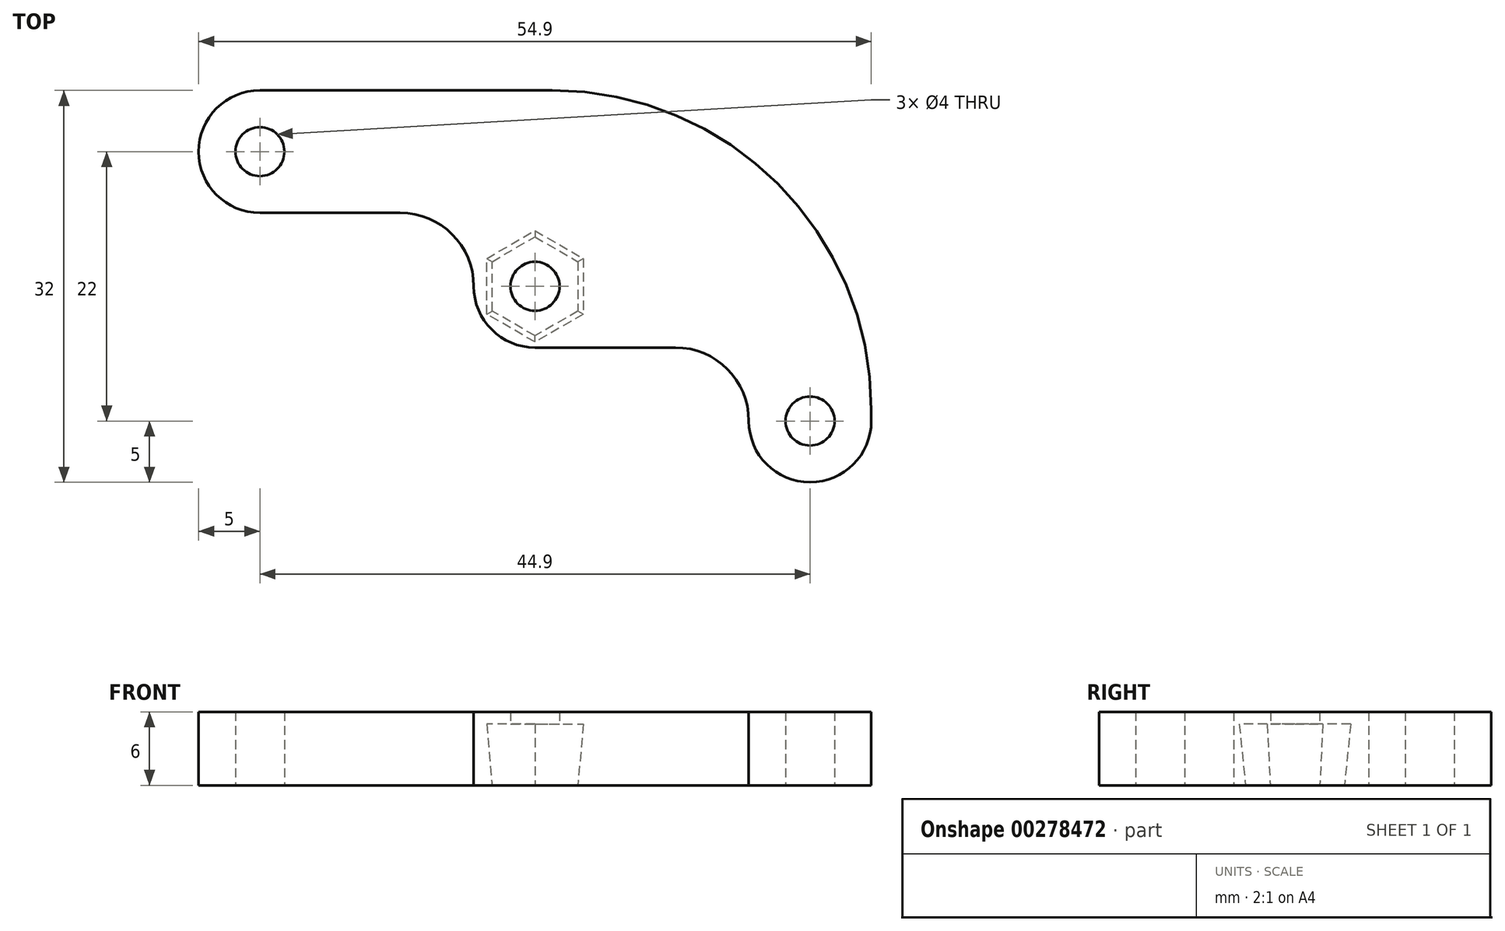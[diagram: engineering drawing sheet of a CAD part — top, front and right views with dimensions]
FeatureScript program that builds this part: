
annotation { "Feature Type Name" : "Feature", "Feature Type Description" : "" }
export const myFeature = defineFeature(function(context is Context, id is Id, definition is map)
    precondition{}
    {
        {
            var Q0;
            Q0=qCreatedBy(makeId("Top.planeOp"),FACE);
            var sketch = newSketch(context, id + "F0", { "sketchPlane" : qUnion([Q0])});
            skCircle(sketch, "E0", {"center": v(0, 0) * mm, "radius": 2 * mm});
            skCircle(sketch, "E1", {"center": v(22.45, -11) * mm, "radius": 2 * mm});
            skCircle(sketch, "E2", {"center": v(-22.45, 11) * mm, "radius": 2 * mm});
            skLineSegment(sketch, "E3", {"start": v(0, 16) * mm, "end": v(0, 6) * mm, "construction": true});
            skLineSegment(sketch, "E4", {"start": v(0, 6) * mm, "end": v(0, -6) * mm, "construction": true});
            skLineSegment(sketch, "E5", {"start": v(0, -6) * mm, "end": v(0, -16) * mm, "construction": true});
            skLineSegment(sketch, "E6", {"start": v(0, 11) * mm, "end": v(-22.45, 11) * mm, "construction": true});
            skLineSegment(sketch, "E7", {"start": v(0, -11) * mm, "end": v(22.45, -11) * mm, "construction": true});
            skCircle(sketch, "E8", {"center": v(-22.45, 11) * mm, "radius": 5 * mm, "construction": true});
            skCircle(sketch, "E9", {"center": v(0, 0) * mm, "radius": 5 * mm, "construction": true});
            skCircle(sketch, "E10", {"center": v(22.45, -11) * mm, "radius": 5 * mm, "construction": true});
            skLineSegment(sketch, "E11", {"start": v(-22.45, 6) * mm, "end": v(-11, 6) * mm});
            skLineSegment(sketch, "E12", {"start": v(-22.45, 16) * mm, "end": v(1.4, 16) * mm});
            skArc(sketch, "E13", {"start": v(-5, 0) * mm, "mid": v(-6.76, 4.24) * mm, "end": v(-11, 6) * mm});
            skArc(sketch, "E14", {"start": v(17.45, -11) * mm, "mid": v(22.45, -16) * mm, "end": v(27.45, -11) * mm});
            skArc(sketch, "E15", {"start": v(-22.45, 16) * mm, "mid": v(-27.45, 11) * mm, "end": v(-22.45, 6) * mm});
            skArc(sketch, "E16", {"start": v(-5, 0) * mm, "mid": v(-3.54, -3.54) * mm, "end": v(0, -5) * mm});
            skLineSegment(sketch, "E17", {"start": v(0, -5) * mm, "end": v(11.45, -5) * mm});
            skArc(sketch, "E18", {"start": v(17.45, -11) * mm, "mid": v(15.7, -6.76) * mm, "end": v(11.45, -5) * mm});
            skLineSegment(sketch, "E19", {"start": v(0, 5) * mm, "end": v(0, 5) * mm});
            skArc(sketch, "E20", {"start": v(27.45, -10.05) * mm, "mid": v(19.82, 8.37) * mm, "end": v(1.4, 16) * mm});
            skLineSegment(sketch, "E21", {"start": v(27.45, -11) * mm, "end": v(27.45, -10.05) * mm});
            skSolve(sketch);
        }
        {
            var Q0;
            Q0=qSketchRegion(id+"F0",true);
            extrude(context, id + "F1", {"entities" : qUnion([Q0]), "depth" : 6 * mm});
        }
        {
            var Q0;
            Q0=makeQuery(id+"F1.opExtrude","CAP_FACE",FACE,{"disambiguationData":[OSD([sQuery(id+"F0.wireOp",EDGE,"E0"),sQuery(id+"F0.wireOp",EDGE,"E1"),sQuery(id+"F0.wireOp",EDGE,"E2"),sQuery(id+"F0.wireOp",EDGE,"E11"),sQuery(id+"F0.wireOp",EDGE,"E12"),sQuery(id+"F0.wireOp",EDGE,"E13"),sQuery(id+"F0.wireOp",EDGE,"E14"),sQuery(id+"F0.wireOp",EDGE,"E15"),sQuery(id+"F0.wireOp",EDGE,"E16"),sQuery(id+"F0.wireOp",EDGE,"E17"),sQuery(id+"F0.wireOp",EDGE,"E18"),sQuery(id+"F0.wireOp",EDGE,"E20"),sQuery(id+"F0.wireOp",EDGE,"E21")])],"isStart":true});
            var sketch = newSketch(context, id + "F2", { "sketchPlane" : qUnion([Q0])});
            skCircle(sketch, "E22.cCircle", {"center": v(0, 0) * mm, "radius": 3.5 * mm, "construction": true});
            skLineSegment(sketch, "E22.0", {"start": v(3.5, -2.02) * mm, "end": v(0, -4.04) * mm});
            skLineSegment(sketch, "E22.1", {"start": v(0, -4.04) * mm, "end": v(-3.5, -2.02) * mm});
            skLineSegment(sketch, "E22.2", {"start": v(-3.5, -2.02) * mm, "end": v(-3.5, 2.02) * mm});
            skLineSegment(sketch, "E22.3", {"start": v(-3.5, 2.02) * mm, "end": v(0, 4.04) * mm});
            skLineSegment(sketch, "E22.4", {"start": v(0, 4.04) * mm, "end": v(3.5, 2.02) * mm});
            skLineSegment(sketch, "E22.5", {"start": v(3.5, 2.02) * mm, "end": v(3.5, -2.02) * mm});
            skPoint(sketch, "E22.0.midPoint", {"position": v(1.75, -3.03) * mm});
            skSolve(sketch);
        }
        {
            var Q0;
            Q0=qSketchRegion(id+"F2",true);
            extrude(context, id + "F3", {"entities" : qUnion([Q0]), "operationType" : NewBodyOperationType.REMOVE, "oppositeDirection" : true, "depth" : 5 * mm, "hasDraft" : true, "draftAngle" : 5 * degree});
        }
    });
